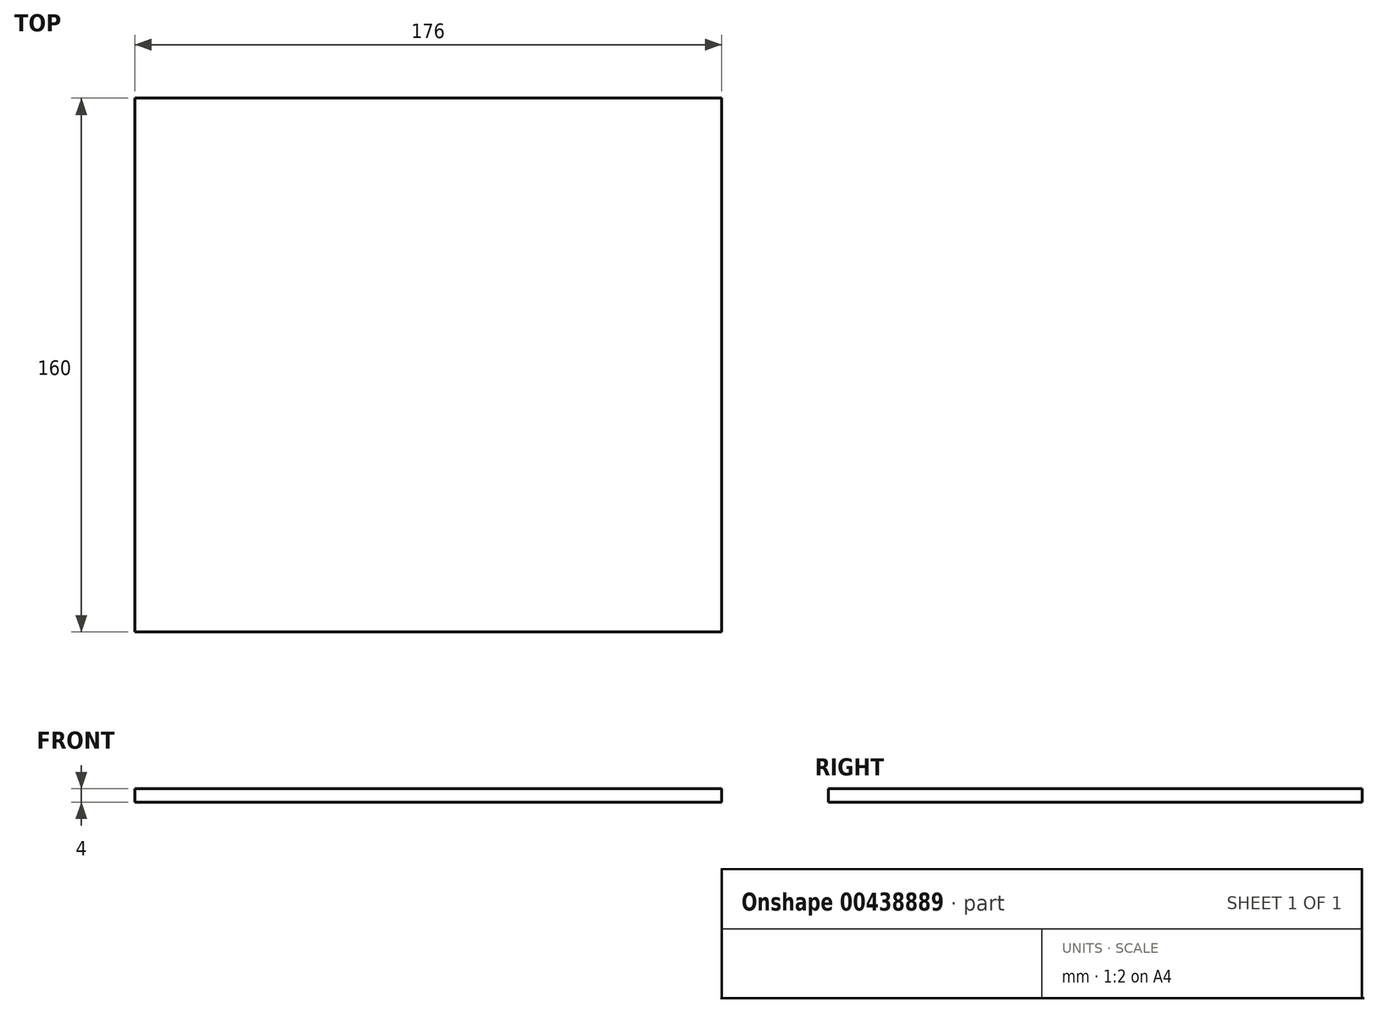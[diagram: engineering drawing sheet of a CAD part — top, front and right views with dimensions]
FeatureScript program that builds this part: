
annotation { "Feature Type Name" : "Feature", "Feature Type Description" : "" }
export const myFeature = defineFeature(function(context is Context, id is Id, definition is map)
    precondition{}
    {
        {
            var Q0;
            Q0=qCreatedBy(makeId("Top.planeOp"),FACE);
            var sketch = newSketch(context, id + "F0", { "sketchPlane" : qUnion([Q0])});
            skLineSegment(sketch, "E0.bottom", {"start": v(88, 80) * mm, "end": v(-88, 80) * mm});
            skLineSegment(sketch, "E0.top", {"start": v(88, -80) * mm, "end": v(-88, -80) * mm});
            skLineSegment(sketch, "E0.left", {"start": v(88, 80) * mm, "end": v(88, -80) * mm});
            skLineSegment(sketch, "E0.right", {"start": v(-88, 80) * mm, "end": v(-88, -80) * mm});
            skPoint(sketch, "E0.middle", {"position": v(0, 0) * mm});
            skSolve(sketch);
        }
        {
            var Q0;
            Q0=makeQuery(id+"F0.imprint","IMPRINT",FACE,{"disambiguationData":[TD([[makeQuery(id+"F0.imprint","IMPRINT",EDGE,{"derivedFrom":sQuery(id+"F0.wireOp",EDGE,"E0.bottom")}),1.0]])]});
            extrude(context, id + "F1", {"entities" : qUnion([Q0]), "depth" : 4 * mm});
        }
    });
